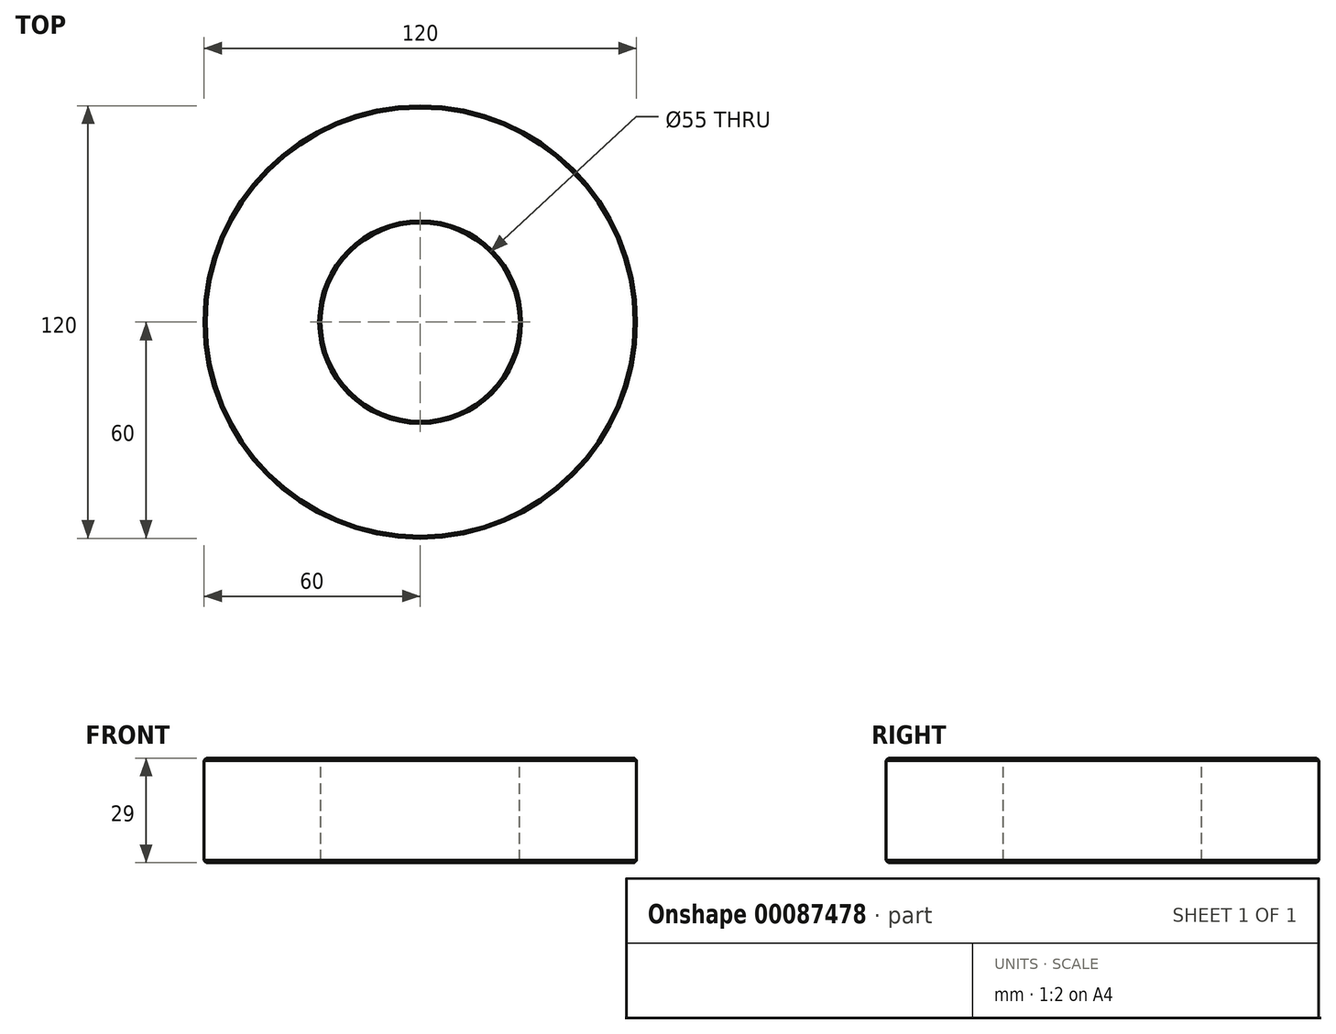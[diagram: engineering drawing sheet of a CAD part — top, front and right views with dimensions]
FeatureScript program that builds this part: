
annotation { "Feature Type Name" : "Feature", "Feature Type Description" : "" }
export const myFeature = defineFeature(function(context is Context, id is Id, definition is map)
    precondition{}
    {
        {
            var Q0;
            Q0=qCreatedBy(makeId("Front.planeOp"),FACE);
            var sketch = newSketch(context, id + "F0", { "sketchPlane" : qUnion([Q0])});
            skLineSegment(sketch, "E0.bottom", {"start": v(-27.5, 14.5) * mm, "end": v(-60, 14.5) * mm});
            skLineSegment(sketch, "E0.top", {"start": v(-27.5, -14.5) * mm, "end": v(-60, -14.5) * mm});
            skLineSegment(sketch, "E0.left", {"start": v(-27.5, 14.5) * mm, "end": v(-27.5, -14.5) * mm});
            skLineSegment(sketch, "E0.right", {"start": v(-60, 14.5) * mm, "end": v(-60, -14.5) * mm});
            skLineSegment(sketch, "E1", {"start": v(0, 56.99) * mm, "end": v(0, -32.1) * mm});
            skSolve(sketch);
        }
        {
            var Q0;
            Q0=makeQuery(id+"F0.imprint","IMPRINT",FACE,{"disambiguationData":[TD([[makeQuery(id+"F0.imprint","IMPRINT",EDGE,{"derivedFrom":sQuery(id+"F0.wireOp",EDGE,"E0.bottom")}),1.0]])]});
            var Q1;
            Q1=sQuery(id+"F0.wireOp",EDGE,"E1");
            revolve(context, id + "F1", {"entities" : qUnion([Q0]), "axis" : qUnion([Q1]), "revolveType" : RevolveType.FULL});
        }
        {
            var Q0;
            Q0=makeQuery(id+"F1.opRevolve","SWEPT_EDGE",EDGE,{"disambiguationData":[OSD([sQuery(id+"F0.wireOp",EDGE,"E0.bottom"),sQuery(id+"F0.wireOp",EDGE,"E0.left")])]});
            var Q1;
            Q1=makeQuery(id+"F1.opRevolve","SWEPT_EDGE",EDGE,{"disambiguationData":[OSD([sQuery(id+"F0.wireOp",EDGE,"E0.bottom"),sQuery(id+"F0.wireOp",EDGE,"E0.right")])]});
            var Q2;
            Q2=makeQuery(id+"F1.opRevolve","SWEPT_EDGE",EDGE,{"disambiguationData":[OSD([sQuery(id+"F0.wireOp",EDGE,"E0.top"),sQuery(id+"F0.wireOp",EDGE,"E0.left")])]});
            var Q3;
            Q3=makeQuery(id+"F1.opRevolve","SWEPT_EDGE",EDGE,{"disambiguationData":[OSD([sQuery(id+"F0.wireOp",EDGE,"E0.top"),sQuery(id+"F0.wireOp",EDGE,"E0.right")])]});
            chamfer(context, id + "F2", {"entities" : qUnion([Q0, Q1, Q2, Q3]), "width" : 0.64 * mm, "tangentPropagation" : true});
        }
    });
